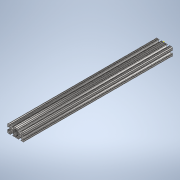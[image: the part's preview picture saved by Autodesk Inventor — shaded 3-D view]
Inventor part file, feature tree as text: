
AUTODESK INVENTOR PART (.ipt)
format: ipt  version: 2020 (Build 240168000, 168)  size: 348,672 bytes
history: native  units: in
note: dims shown in document units (in); Inventor stores cm internally (conversion verified against a paired STEP export)
features: sketch x2, extrude x1
ambient origin geometry x8: Origin, YZ Plane, XZ Plane, XY Plane, X Axis, Y Axis, Z Axis, Center Point
bodies: Solid1 (feature_tree)
feature tree (3):
  extrude  "Extrusion1"  [1 undecoded]
  sketch  "Sketch2"
  sketch  "Sketch1"  dims[d0=18.0in d1=0.0in]
note: 1 required parameter value undecoded (feature->parameter linkage not recoverable at this tier; creation-order binding heuristic only, values carry confidence <= 0.55)
